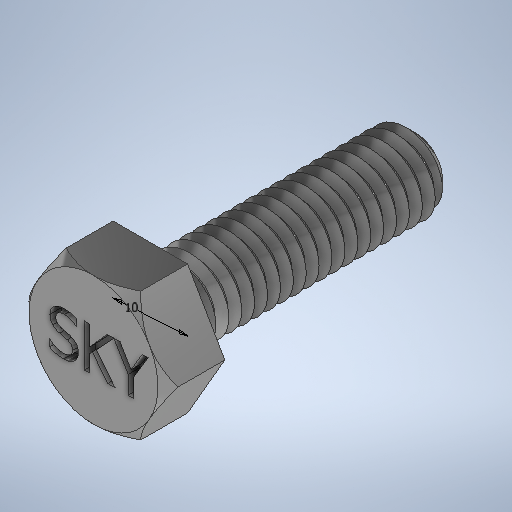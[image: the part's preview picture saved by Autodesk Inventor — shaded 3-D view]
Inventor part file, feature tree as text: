
AUTODESK INVENTOR PART (.ipt)
format: ipt  version: 2025.2 (Build 292293000, 293)  size: 727,040 bytes
history: native  units: in
note: dims shown in document units (in); Inventor stores cm internally (conversion verified against a paired STEP export)
features: sketch x6, extrude x3, chamfer x1, fillet x1, helix x1, emboss x1
ambient origin geometry x8: Origin, YZ Plane, XZ Plane, XY Plane, X Axis, Y Axis, Z Axis, Center Point
bodies: Solid1 (feature_tree)
feature tree (13):
  extrude  "Extrusion1"  Depth=0.6693in
  extrude  "Extrusion2"  TaperAngle=0.0deg  [1 undecoded]
  extrude  "Extrusion3"  Depth=1.378in TaperAngle=0.0deg
  chamfer  "Chamfer1"  Distance=0.0591in Angle=45.0deg
  fillet  "Fillet1"  Radius=0.0197in
  sketch  "Sketch4"  dims[d15=0.0787in]
  helix  "Coil1"  [1 undecoded]
  emboss  "Emboss1"
  sketch  "Sketch1"  dims[d1=0.6693in d2=0.6693in]
  sketch  "Sketch2"  dims[d3=0.2953in d4=0.0in d5=0.0in d6=45.0deg]
  sketch  "Sketch3"  dims[d7=0.3937in d8=1.378in d9=0.0in d10=0.0591in d11=0.0787in d12=45.0deg d13=0.0197in d14=0.0669in]
  sketch  "Sketch5"  dims[d16=60.0deg]
  sketch  "Sketch6"  dims[d17=0.0079in d18=0.0669in d19=1.378in d20=0.3937in d21=0.0in d22=90.0deg d23=90.0deg d24=90.0deg d25=0.0in d26=0.0591in d27=0.0344in]
note: 2 required parameter values undecoded (feature->parameter linkage not recoverable at this tier; creation-order binding heuristic only, values carry confidence <= 0.55)
